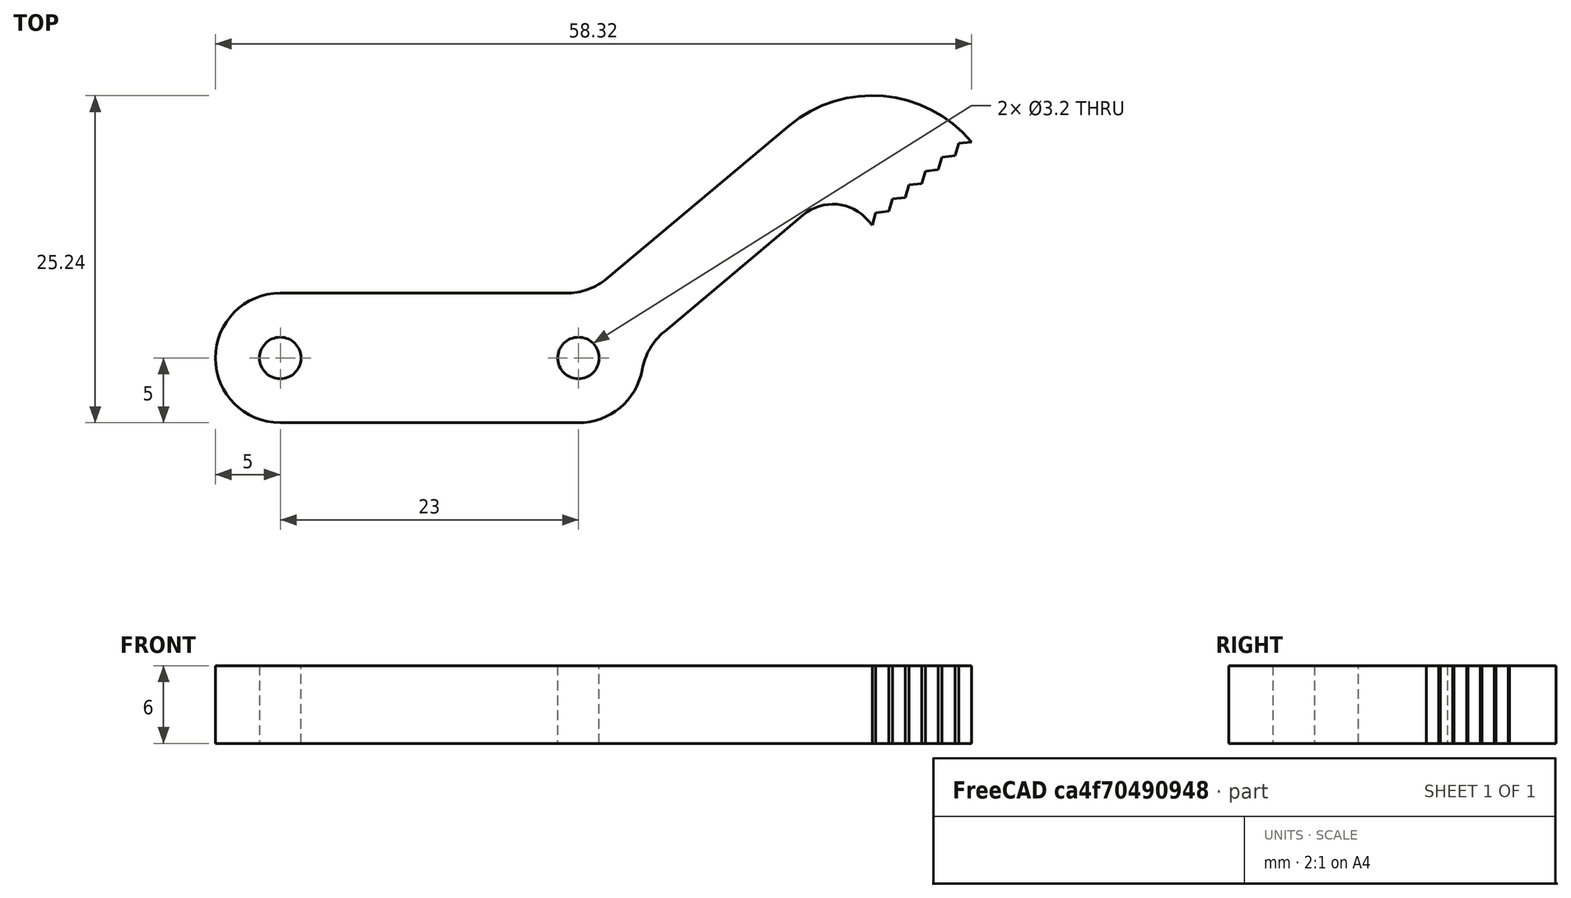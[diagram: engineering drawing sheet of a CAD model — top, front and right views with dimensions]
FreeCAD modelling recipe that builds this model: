
FCSTD DOCUMENT  (FreeCAD 0.19R24276 (Git))
Label: part2
License: All rights reserved
LicenseURL: http://en.wikipedia.org/wiki/All_rights_reserved
objects: Sketcher::SketchObject×1, PartDesign::Pad×1, PartDesign::Body×1
note: 4 computed .brp shape members not serialized (recipe doc carries the construction recipe); baked Part::Feature solids carry a one-line shape summary decoded from their .brp

FEATURE [Sketcher::SketchObject] Sketch
  FullyConstrained = false
  MapMode = 5
  Support = -> [XY_Plane]
  sketch-geometry (28):
    g0: ArcOfCircle CenterX=0 CenterY=0 CenterZ=0 NormalX=0 NormalY=0 NormalZ=1 AngleXU=0 Radius=5 StartAngle=1.5708 EndAngle=4.71239
    g1: ArcOfCircle CenterX=23 CenterY=4e-16 CenterZ=0 NormalX=0 NormalY=0 NormalZ=1 AngleXU=0 Radius=5 StartAngle=4.71239 EndAngle=6.09993
    g2: LineSegment StartX=-9e-16 StartY=-5 StartZ=0 EndX=23 EndY=-5 EndZ=0
    g3: LineSegment StartX=-8e-16 StartY=5 StartZ=0 EndX=22.03 EndY=5 EndZ=0
    g4: ArcOfCircle CenterX=45.6544 CenterY=10.2421 CenterZ=0 NormalX=0 NormalY=0 NormalZ=1 AngleXU=0 Radius=10 StartAngle=0.697735 EndAngle=2.2686
    g5: ArcOfCircle CenterX=22.03 CenterY=10 CenterZ=0 NormalX=0 NormalY=0 NormalZ=1 AngleXU=0 Radius=5 StartAngle=4.71239 EndAngle=5.41014
    g6: ArcOfCircle CenterX=32.8326 CenterY=-1.82231 CenterZ=0 NormalX=0 NormalY=0 NormalZ=1 AngleXU=0 Radius=5 StartAngle=2.26853 EndAngle=2.95834
    g7: Circle CenterX=0 CenterY=0 CenterZ=0 NormalX=0 NormalY=0 NormalZ=1 AngleXU=0 Radius=1.6
    g8: Circle CenterX=23 CenterY=4e-16 CenterZ=0 NormalX=0 NormalY=0 NormalZ=1 AngleXU=0 Radius=1.6
    g9: LineSegment StartX=45.6544 StartY=10.2421 StartZ=0 EndX=45.9378 EndY=11.2011 EndZ=0
    g10: LineSegment StartX=45.9378 StartY=11.2011 StartZ=0 EndX=46.9316 EndY=11.3129 EndZ=0
    g11: LineSegment StartX=46.9316 StartY=11.3129 StartZ=0 EndX=47.215 EndY=12.2719 EndZ=0
    g12: LineSegment StartX=47.215 StartY=12.2719 StartZ=0 EndX=48.2087 EndY=12.3837 EndZ=0
    g13: LineSegment StartX=48.2087 StartY=12.3837 StartZ=0 EndX=48.4922 EndY=13.3427 EndZ=0
    g14: LineSegment StartX=48.4922 StartY=13.3427 StartZ=0 EndX=49.4859 EndY=13.4545 EndZ=0
    g15: LineSegment StartX=49.4859 StartY=13.4545 StartZ=0 EndX=49.7693 EndY=14.4135 EndZ=0
    g16: LineSegment StartX=49.7693 StartY=14.4135 StartZ=0 EndX=50.7631 EndY=14.5253 EndZ=0
    g17: LineSegment StartX=50.7631 StartY=14.5253 StartZ=0 EndX=51.0465 EndY=15.4843 EndZ=0
    g18: LineSegment StartX=51.0465 StartY=15.4843 StartZ=0 EndX=52.0402 EndY=15.5962 EndZ=0
    g19: LineSegment StartX=52.0402 StartY=15.5962 StartZ=0 EndX=52.3237 EndY=16.5551 EndZ=0
    g20: LineSegment StartX=52.3237 StartY=16.5551 StartZ=0 EndX=53.3174 EndY=16.667 EndZ=0
    g21: GeomPoint X=-5 Y=0 Z=0
    g22: LineSegment StartX=45.6544 StartY=10.2421 StartZ=0 EndX=46.9316 EndY=11.3129 EndZ=0
    g23: LineSegment StartX=45.6544 StartY=10.2421 StartZ=0 EndX=45.387 EndY=10.5611 EndZ=0
    g24: ArcOfCircle CenterX=42.6462 CenterY=8.26323 CenterZ=0 NormalX=0 NormalY=0 NormalZ=1 AngleXU=0 Radius=3.57658 StartAngle=0.697735 EndAngle=2.26853
    g25: LineSegment StartX=25.2425 StartY=6.16854 StartZ=0 EndX=39.2069 EndY=17.877 EndZ=0
    g26: LineSegment StartX=31.4813 StartY=11.3995 StartZ=0 EndX=35.3363 EndY=6.80172 EndZ=0
    g27: LineSegment StartX=29.6201 StartY=2.00919 StartZ=0 EndX=40.3483 EndY=11.004 EndZ=0
  constraints (67):
    c: Tangent(g0,g3) = 1.5708
    c: Tangent(g0,g2) = -1.5708
    c: Tangent(g2,g1) = -1.5708
    c: Horizontal(g2)
    c: Equal(g0,g1)
    c: Coincident(g0,g-1)
    c: DistanceX(g0,g1) = 23
    c: Tangent(g3,g5) = -1.5708
    c: Tangent(g1,g6) = 1.5708
    c: Coincident(g7,g0)
    c: Coincident(g8,g1)
    c: Equal(g8,g7)
    c: Horizontal(g3)
    c: Distance(g4,g4) = 10
    c: DistanceY(g0,g0) = 10
    c: Coincident(g9,g4)
    c: Coincident(g9,g10)
    c: Coincident(g10,g11)
    c: Coincident(g11,g12)
    c: Coincident(g12,g13)
    c: Coincident(g13,g14)
    c: Coincident(g14,g15)
    c: Coincident(g15,g16)
    c: Coincident(g16,g17)
    c: Coincident(g17,g18)
    c: Coincident(g18,g19)
    c: Coincident(g19,g20)
    c: Coincident(g20,g4)
    c: Equal(g19,g17)
    c: Equal(g20,g19)
    c: Equal(g18,g20)
    c: Equal(g16,g20)
    c: Equal(g19,g15)
    c: Equal(g14,g20)
    c: Equal(g13,g19)
    c: Equal(g12,g14)
    c: Equal(g13,g11)
    c: Equal(g10,g12)
    c: Equal(g11,g9)
    c: Parallel(g19,g17)
    c: Parallel(g17,g15)
    c: Parallel(g15,g13)
    c: Parallel(g13,g11)
    c: Parallel(g11,g9)
    c: Diameter(g7) = 3.2
    c: PointOnObject(g21,g0)
    c: PointOnObject(g21,g-1)
    c: Parallel(g10,g12)
    c: Parallel(g12,g14)
    c: Parallel(g14,g16)
    c: Parallel(g16,g18)
    c: Parallel(g18,g20)
    c: DistanceX(g3,g3) = 22.03
    c: Distance(g11,g12) = 1
    c: Coincident(g22,g4)
    c: Coincident(g22,g10)
    c: Equal(g5,g1)
    c: Equal(g6,g1)
    c: Coincident(g23,g4)
    c: Tangent(g23,g24) = -1.5708
    c: Tangent(g5,g25) = -1.5708
    c: PointOnObject(g26,g25)
    c: Perpendicular(g26,g25)
    c: Distance(g26) = 6
    c: Coincident(g27,g6)
    c: Coincident(g27,g24)
    c: Distance(g27) = 14
FEATURE [PartDesign::Pad] Pad
  Direction = (1,1,1)
  Length = 6
  Length2 = 100
  Profile = -> Sketch
  Type = 0
FEATURE [PartDesign::Body] Body
  Group = -> [Sketch,Pad]
  Origin = -> Origin
  Tip = -> Pad
